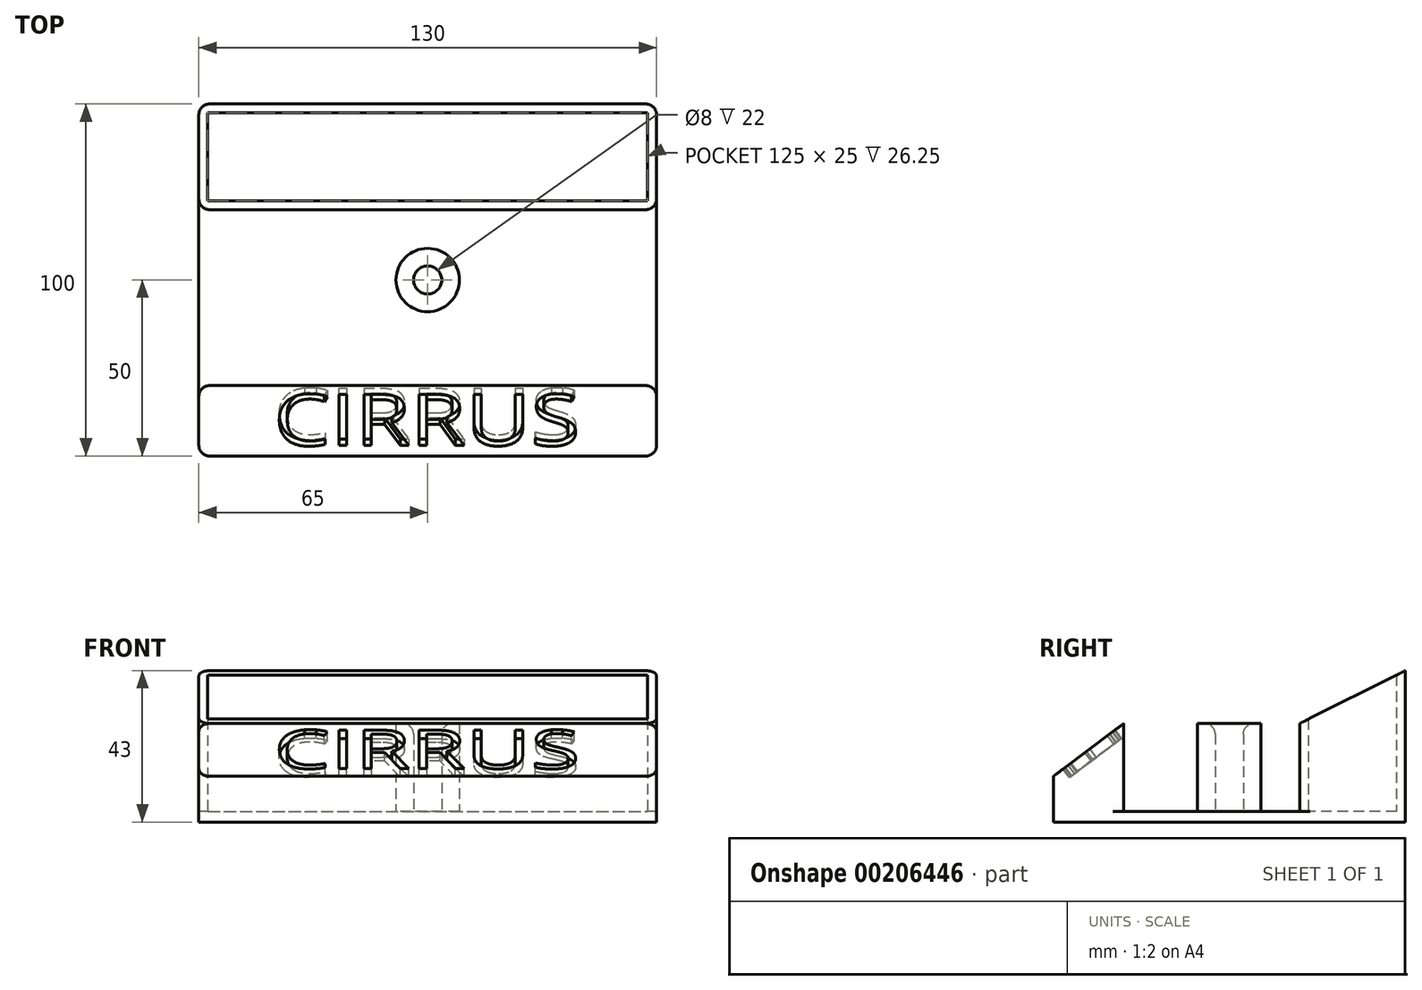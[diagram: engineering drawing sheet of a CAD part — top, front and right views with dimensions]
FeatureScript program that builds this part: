
annotation { "Feature Type Name" : "Feature", "Feature Type Description" : "" }
export const myFeature = defineFeature(function(context is Context, id is Id, definition is map)
    precondition{}
    {
        {
            var Q0;
            Q0=qCreatedBy(makeId("Top.planeOp"),FACE);
            var sketch = newSketch(context, id + "F0", { "sketchPlane" : qUnion([Q0])});
            skLineSegment(sketch, "E0.bottom", {"start": v(-65, 100) * mm, "end": v(65, 100) * mm});
            skLineSegment(sketch, "E0.top", {"start": v(-65, 0) * mm, "end": v(65, 0) * mm});
            skLineSegment(sketch, "E0.left", {"start": v(65, 100) * mm, "end": v(65, 0) * mm});
            skLineSegment(sketch, "E0.right", {"start": v(-65, 100) * mm, "end": v(-65, 0) * mm});
            skSolve(sketch);
        }
        {
            var Q0;
            Q0=makeQuery(id+"F0.imprint","IMPRINT",FACE,{"disambiguationData":[TD([[makeQuery(id+"F0.imprint","IMPRINT",EDGE,{"derivedFrom":sQuery(id+"F0.wireOp",EDGE,"E0.bottom")}),-1.0]])]});
            extrude(context, id + "F1", {"entities" : qUnion([Q0]), "depth" : 3 * mm});
        }
        {
            var Q0;
            Q0=makeQuery(id+"F1.opExtrude","CAP_FACE",FACE,{"disambiguationData":[OSD([sQuery(id+"F0.wireOp",EDGE,"E0.bottom"),sQuery(id+"F0.wireOp",EDGE,"E0.top"),sQuery(id+"F0.wireOp",EDGE,"E0.left"),sQuery(id+"F0.wireOp",EDGE,"E0.right")])],"isStart":false});
            var sketch = newSketch(context, id + "F2", { "sketchPlane" : qUnion([Q0])});
            skLineSegment(sketch, "E1", {"start": v(0, 0) * mm, "end": v(0, 100) * mm, "construction": true});
            skCircle(sketch, "E2", {"center": v(0, 50) * mm, "radius": 9 * mm});
            skCircle(sketch, "E3", {"center": v(0, 50) * mm, "radius": 4 * mm});
            skLineSegment(sketch, "E4.bottom", {"start": v(-65, 0) * mm, "end": v(65, 0) * mm});
            skLineSegment(sketch, "E4.top", {"start": v(-65, 20) * mm, "end": v(65, 20) * mm});
            skLineSegment(sketch, "E4.left", {"start": v(-65, 0) * mm, "end": v(-65, 20) * mm});
            skLineSegment(sketch, "E4.right", {"start": v(65, 0) * mm, "end": v(65, 20) * mm});
            skLineSegment(sketch, "E5.bottom", {"start": v(-65, 100) * mm, "end": v(65, 100) * mm});
            skLineSegment(sketch, "E5.top", {"start": v(-65, 70) * mm, "end": v(65, 70) * mm});
            skLineSegment(sketch, "E5.left", {"start": v(-65, 100) * mm, "end": v(-65, 70) * mm});
            skLineSegment(sketch, "E5.right", {"start": v(65, 100) * mm, "end": v(65, 70) * mm});
            skLineSegment(sketch, "E6.0", {"start": v(62.5, 97.5) * mm, "end": v(62.5, 72.5) * mm});
            skLineSegment(sketch, "E6.1", {"start": v(-62.5, 97.5) * mm, "end": v(62.5, 97.5) * mm});
            skLineSegment(sketch, "E6.2", {"start": v(-62.5, 97.5) * mm, "end": v(-62.5, 72.5) * mm});
            skLineSegment(sketch, "E6.3", {"start": v(-62.5, 72.5) * mm, "end": v(62.5, 72.5) * mm});
            skSolve(sketch);
        }
        {
            var Q0;
            Q0=makeQuery(id+"F2.imprint","IMPRINT",FACE,{"disambiguationData":[TD([[makeQuery(id+"F2.imprint","IMPRINT",EDGE,{"derivedFrom":sQuery(id+"F2.wireOp",EDGE,"E5.bottom")}),-1.0]])]});
            extrude(context, id + "F3", {"entities" : qUnion([Q0]), "operationType" : NewBodyOperationType.ADD, "depth" : 40 * mm});
        }
        {
            var Q0;
            Q0=makeQuery(id+"F2.imprint","IMPRINT",FACE,{"disambiguationData":[TD([[makeQuery(id+"F2.imprint","IMPRINT",EDGE,{"derivedFrom":sQuery(id+"F2.wireOp",EDGE,"E2")}),1.0]])]});
            var Q1;
            Q1=makeQuery(id+"F2.imprint","IMPRINT",FACE,{"disambiguationData":[TD([[makeQuery(id+"F2.imprint","IMPRINT",EDGE,{"derivedFrom":sQuery(id+"F2.wireOp",EDGE,"E4.bottom")}),1.0]])]});
            extrude(context, id + "F4", {"entities" : qUnion([Q0, Q1]), "operationType" : NewBodyOperationType.ADD, "depth" : 25 * mm});
        }
        {
            var Q0;
            Q0=makeQuery(id+"F4.opExtrude","CAP_EDGE",EDGE,{"disambiguationData":[OSD([sQuery(id+"F2.wireOp",EDGE,"E4.bottom")])],"isStart":false});
            chamfer(context, id + "F5", {"entities" : qUnion([Q0]), "chamferType" : ChamferType.TWO_OFFSETS, "width1" : 20 * mm, "oppositeDirection" : false, "width2" : 15 * mm, "tangentPropagation" : true});
        }
        {
            var Q0;
            Q0=makeQuery(id+"F3.opExtrude","CAP_EDGE",EDGE,{"disambiguationData":[OSD([sQuery(id+"F2.wireOp",EDGE,"E5.top")])],"isStart":false});
            chamfer(context, id + "F6", {"entities" : qUnion([Q0]), "chamferType" : ChamferType.TWO_OFFSETS, "width1" : 30 * mm, "oppositeDirection" : false, "width2" : 15 * mm, "tangentPropagation" : true});
        }
        {
            var Q0;
            Q0=makeQuery(id+"F3.boolean.opBoolean","MERGE",EDGE,{"derivedFrom":[makeQuery(id+"F1.opExtrude","SWEPT_EDGE",EDGE,{"disambiguationData":[OSD([sQuery(id+"F0.wireOp",EDGE,"E0.bottom"),sQuery(id+"F0.wireOp",EDGE,"E0.right")])]}),makeQuery(id+"F3.opExtrude","SWEPT_EDGE",EDGE,{"disambiguationData":[OSD([sQuery(id+"F2.wireOp",EDGE,"E5.bottom"),sQuery(id+"F2.wireOp",EDGE,"E5.left")])]})]});
            var Q1;
            Q1=makeQuery(id+"F3.opExtrude","SWEPT_EDGE",EDGE,{"disambiguationData":[OSD([sQuery(id+"F0.wireOp",EDGE,"E0.right"),sQuery(id+"F2.wireOp",EDGE,"E5.top"),sQuery(id+"F2.wireOp",EDGE,"E5.left")])]});
            var Q2;
            Q2=makeQuery(id+"F3.opExtrude","SWEPT_EDGE",EDGE,{"disambiguationData":[OSD([sQuery(id+"F0.wireOp",EDGE,"E0.left"),sQuery(id+"F2.wireOp",EDGE,"E5.top"),sQuery(id+"F2.wireOp",EDGE,"E5.right")])]});
            var Q3;
            Q3=makeQuery(id+"F4.boolean.opBoolean","MERGE",EDGE,{"derivedFrom":[makeQuery(id+"F1.opExtrude","SWEPT_EDGE",EDGE,{"disambiguationData":[OSD([sQuery(id+"F0.wireOp",EDGE,"E0.top"),sQuery(id+"F0.wireOp",EDGE,"E0.right")])]}),makeQuery(id+"F4.opExtrude","SWEPT_EDGE",EDGE,{"disambiguationData":[OSD([sQuery(id+"F2.wireOp",EDGE,"E4.bottom"),sQuery(id+"F2.wireOp",EDGE,"E4.left")])]})]});
            var Q4;
            Q4=makeQuery(id+"F3.boolean.opBoolean","MERGE",EDGE,{"derivedFrom":[makeQuery(id+"F1.opExtrude","SWEPT_EDGE",EDGE,{"disambiguationData":[OSD([sQuery(id+"F0.wireOp",EDGE,"E0.bottom"),sQuery(id+"F0.wireOp",EDGE,"E0.left")])]}),makeQuery(id+"F3.opExtrude","SWEPT_EDGE",EDGE,{"disambiguationData":[OSD([sQuery(id+"F2.wireOp",EDGE,"E5.bottom"),sQuery(id+"F2.wireOp",EDGE,"E5.right")])]})]});
            var Q5;
            Q5=makeQuery(id+"F4.boolean.opBoolean","MERGE",EDGE,{"derivedFrom":[makeQuery(id+"F1.opExtrude","SWEPT_EDGE",EDGE,{"disambiguationData":[OSD([sQuery(id+"F0.wireOp",EDGE,"E0.top"),sQuery(id+"F0.wireOp",EDGE,"E0.left")])]}),makeQuery(id+"F4.opExtrude","SWEPT_EDGE",EDGE,{"disambiguationData":[OSD([sQuery(id+"F2.wireOp",EDGE,"E4.bottom"),sQuery(id+"F2.wireOp",EDGE,"E4.right")])]})]});
            var Q6;
            Q6=makeQuery(id+"F4.opExtrude","SWEPT_EDGE",EDGE,{"disambiguationData":[OSD([sQuery(id+"F0.wireOp",EDGE,"E0.left"),sQuery(id+"F2.wireOp",EDGE,"E4.top"),sQuery(id+"F2.wireOp",EDGE,"E4.right")])]});
            var Q7;
            Q7=makeQuery(id+"F4.opExtrude","SWEPT_EDGE",EDGE,{"disambiguationData":[OSD([sQuery(id+"F0.wireOp",EDGE,"E0.right"),sQuery(id+"F2.wireOp",EDGE,"E4.top"),sQuery(id+"F2.wireOp",EDGE,"E4.left")])]});
            var Q8;
            Q8=makeQuery(id+"F4.opExtrude","CAP_EDGE",EDGE,{"disambiguationData":[OSD([sQuery(id+"F2.wireOp",EDGE,"E3")])],"isStart":false});
            fillet(context, id + "F7", {"entities" : qUnion([Q0, Q1, Q2, Q3, Q4, Q5, Q6, Q7, Q8]), "radius" : 3 * mm, "tangentPropagation" : true, "allowEdgeOverflow" : false});
        }
        {
            var Q0;
            Q0=makeQuery(id+"F5.opChamfer","BLEND_FACE",FACE,{"disambiguationData":[OSD([sQuery(id+"F2.wireOp",EDGE,"E4.bottom")])]});
            var sketch = newSketch(context, id + "F8", { "sketchPlane" : qUnion([Q0])});
            skLineSegment(sketch, "E7.0", {"start": v(62, 10.8) * mm, "end": v(-62, 10.8) * mm});
            skLineSegment(sketch, "E8.0", {"start": v(-62, 29.8) * mm, "end": v(62, 29.8) * mm});
            skText(sketch, "E9", { "text": "CIRRUS", "fontName": "OpenSans-Regular.ttf"});
            skLineSegment(sketch, "E10", {"start": v(-62, 10.8) * mm, "end": v(-62, 47.82) * mm});
            skLineSegment(sketch, "E11", {"start": v(62, 10.8) * mm, "end": v(62, 49.07) * mm});
            skPoint(sketch, "E11.endSnap0", {"position": v(62, 15.3) * mm});
            const initialGuessF8  = {"E9": [-0.04369, 0.01151, 1, 0, 0.01829]};
            skSetInitialGuess(sketch, initialGuessF8);
            skSolve(sketch);
        }
        {
            var Q0;
            Q0=makeQuery(id+"F8.imprint","IMPRINT",FACE,{"disambiguationData":[TD([[makeQuery(id+"F8.imprint","IMPRINT",EDGE,{"derivedFrom":sQuery(id+"F8.wireOp",EDGE,"E9.sketch_text.stroke-0")}),-1.0]])]});
            var Q1;
            Q1=makeQuery(id+"F8.imprint","IMPRINT",FACE,{"disambiguationData":[TD([[makeQuery(id+"F8.imprint","IMPRINT",EDGE,{"derivedFrom":sQuery(id+"F8.wireOp",EDGE,"E9.sketch_text.stroke-13")}),-1.0]])]});
            var Q2;
            Q2=makeQuery(id+"F8.imprint","IMPRINT",FACE,{"disambiguationData":[TD([[makeQuery(id+"F8.imprint","IMPRINT",EDGE,{"derivedFrom":sQuery(id+"F8.wireOp",EDGE,"E9.sketch_text.stroke-19")}),-1.0]])]});
            var Q3;
            Q3=makeQuery(id+"F8.imprint","IMPRINT",FACE,{"disambiguationData":[TD([[makeQuery(id+"F8.imprint","IMPRINT",EDGE,{"derivedFrom":sQuery(id+"F8.wireOp",EDGE,"E9.sketch_text.stroke-27")}),-1.0]])]});
            var Q4;
            Q4=makeQuery(id+"F8.imprint","IMPRINT",FACE,{"disambiguationData":[TD([[makeQuery(id+"F8.imprint","IMPRINT",EDGE,{"derivedFrom":sQuery(id+"F8.wireOp",EDGE,"E9.sketch_text.stroke-43")}),-1.0]])]});
            var Q5;
            Q5=makeQuery(id+"F8.imprint","IMPRINT",FACE,{"disambiguationData":[TD([[makeQuery(id+"F8.imprint","IMPRINT",EDGE,{"derivedFrom":sQuery(id+"F8.wireOp",EDGE,"E9.sketch_text.stroke-58")}),-1.0]])]});
            var Q6;
            Q6=makeQuery(id+"F8.imprint","IMPRINT",FACE,{"disambiguationData":[TD([[makeQuery(id+"F8.imprint","IMPRINT",EDGE,{"derivedFrom":sQuery(id+"F8.wireOp",EDGE,"E9.sketch_text.stroke-72")}),-1.0]])]});
            var Q7;
            Q7=makeQuery(id+"F8.imprint","IMPRINT",FACE,{"disambiguationData":[TD([[makeQuery(id+"F8.imprint","IMPRINT",EDGE,{"derivedFrom":sQuery(id+"F8.wireOp",EDGE,"E9.sketch_text.stroke-90")}),-1.0]])]});
            var Q8;
            Q8=makeQuery(id+"F8.imprint","IMPRINT",FACE,{"disambiguationData":[TD([[makeQuery(id+"F8.imprint","IMPRINT",EDGE,{"derivedFrom":sQuery(id+"F8.wireOp",EDGE,"E9.sketch_text.stroke-15")}),-1.0]])]});
            var Q9;
            Q9=makeQuery(id+"F8.imprint","IMPRINT",FACE,{"disambiguationData":[TD([[makeQuery(id+"F8.imprint","IMPRINT",EDGE,{"derivedFrom":sQuery(id+"F8.wireOp",EDGE,"E9.sketch_text.stroke-55")}),-1.0]])]});
            extrude(context, id + "F9", {"entities" : qUnion([Q0, Q1, Q2, Q3, Q4, Q5, Q6, Q7, Q8, Q9]), "operationType" : NewBodyOperationType.REMOVE, "oppositeDirection" : true, "depth" : 3 * mm});
        }
    });
